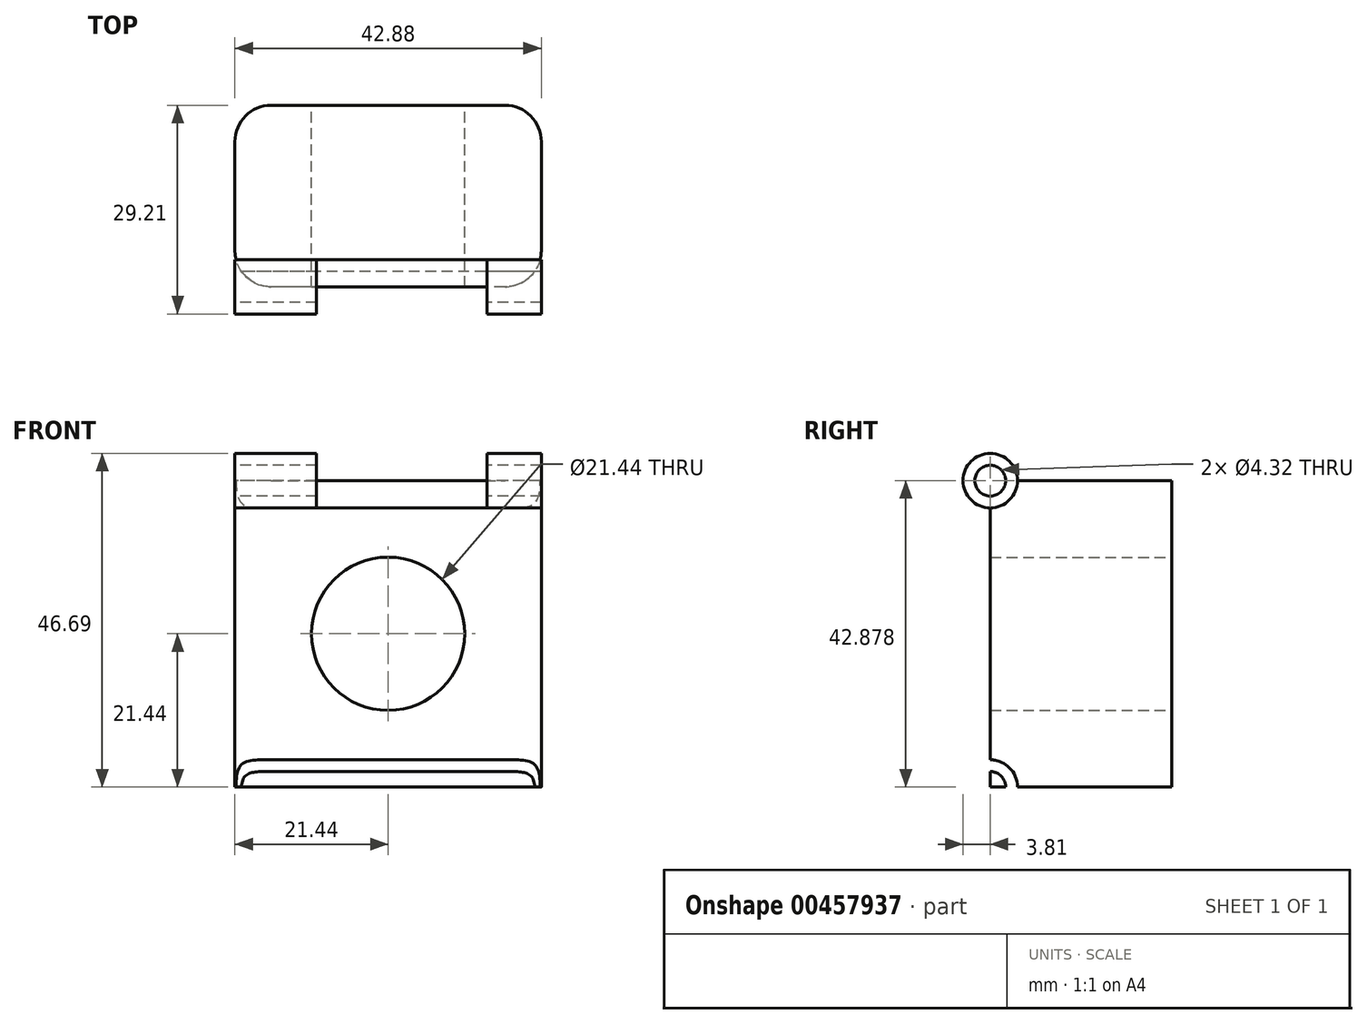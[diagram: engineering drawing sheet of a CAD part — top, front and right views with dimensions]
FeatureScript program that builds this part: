
annotation { "Feature Type Name" : "Feature", "Feature Type Description" : "" }
export const myFeature = defineFeature(function(context is Context, id is Id, definition is map)
    precondition{}
    {
        {
            var Q0;
            Q0=qCreatedBy(makeId("Front.planeOp"),FACE);
            var sketch = newSketch(context, id + "F0", { "sketchPlane" : qUnion([Q0])});
            skLineSegment(sketch, "E0.bottom", {"start": v(-21.44, 21.44) * mm, "end": v(21.44, 21.44) * mm});
            skLineSegment(sketch, "E0.top", {"start": v(-21.44, -21.44) * mm, "end": v(21.44, -21.44) * mm});
            skLineSegment(sketch, "E0.left", {"start": v(-21.44, 21.44) * mm, "end": v(-21.44, -21.44) * mm});
            skLineSegment(sketch, "E0.right", {"start": v(21.44, 21.44) * mm, "end": v(21.44, -21.44) * mm});
            skPoint(sketch, "E0.middle", {"position": v(0, 0) * mm});
            skCircle(sketch, "E1", {"center": v(0, 0) * mm, "radius": 10.72 * mm});
            skSolve(sketch);
        }
        {
            var Q0;
            Q0=makeQuery(id+"F0.imprint","IMPRINT",FACE,{"disambiguationData":[TD([[makeQuery(id+"F0.imprint","IMPRINT",EDGE,{"derivedFrom":sQuery(id+"F0.wireOp",EDGE,"E0.bottom")}),-1.0]])]});
            extrude(context, id + "F1", {"entities" : qUnion([Q0]), "depth" : 25.4 * mm, "offsetDistance" : 25.4 * mm});
        }
        {
            var Q0;
            Q0=makeQuery(id+"F1.opExtrude","CAP_EDGE",EDGE,{"disambiguationData":[OSD([sQuery(id+"F0.wireOp",EDGE,"E0.right")])],"isStart":true});
            var Q1;
            Q1=makeQuery(id+"F1.opExtrude","CAP_EDGE",EDGE,{"disambiguationData":[OSD([sQuery(id+"F0.wireOp",EDGE,"E0.right")])],"isStart":false});
            var Q2;
            Q2=makeQuery(id+"F1.opExtrude","CAP_EDGE",EDGE,{"disambiguationData":[OSD([sQuery(id+"F0.wireOp",EDGE,"E0.left")])],"isStart":true});
            var Q3;
            Q3=makeQuery(id+"F1.opExtrude","CAP_EDGE",EDGE,{"disambiguationData":[OSD([sQuery(id+"F0.wireOp",EDGE,"E0.left")])],"isStart":false});
            fillet(context, id + "F2", {"entities" : qUnion([Q0, Q1, Q2, Q3]), "radius" : 5.08 * mm, "tangentPropagation" : true, "allowEdgeOverflow" : false});
        }
        {
            var Q0;
            Q0=makeQuery(id+"F1.opExtrude","SWEPT_FACE",FACE,{"disambiguationData":[OSD([sQuery(id+"F0.wireOp",EDGE,"E0.left")])]});
            var sketch = newSketch(context, id + "F3", { "sketchPlane" : qUnion([Q0])});
            skPoint(sketch, "E2.0", {"position": v(25.4, 21.44) * mm});
            skPoint(sketch, "E3.0", {"position": v(25.4, -21.44) * mm});
            skCircle(sketch, "E4", {"center": v(25.4, 21.44) * mm, "radius": 3.81 * mm});
            skCircle(sketch, "E5.MirrorC", {"center": v(25.4, -21.44) * mm, "radius": 3.81 * mm});
            skCircle(sketch, "E6", {"center": v(25.4, 21.44) * mm, "radius": 2.16 * mm});
            skCircle(sketch, "E7.MirrorC", {"center": v(25.4, -21.44) * mm, "radius": 2.16 * mm});
            skSolve(sketch);
        }
        {
            var Q0;
            Q0 = qSketchRegion(id + "F3", true);
            var Q1;
            Q1=makeQuery(id+"F3.imprint","IMPRINT",FACE,{"disambiguationData":[TD([[makeQuery(id+"F3.imprint","IMPRINT",EDGE,{"derivedFrom":sQuery(id+"F3.wireOp",EDGE,"E6")}),1.0]])]});
            extrude(context, id + "F4", {"entities" : qUnion([Q0, Q1]), "operationType" : NewBodyOperationType.ADD, "oppositeDirection" : true, "depth" : 42.88 * mm, "offsetDistance" : 25.4 * mm});
        }
        {
            var Q0;
            Q0=makeQuery(id+"F3.imprint","IMPRINT",FACE,{"disambiguationData":[TD([[makeQuery(id+"F3.imprint","IMPRINT",EDGE,{"derivedFrom":sQuery(id+"F3.wireOp",EDGE,"E6")}),1.0]])]});
            extrude(context, id + "F5", {"entities" : qUnion([Q0]), "operationType" : NewBodyOperationType.REMOVE, "oppositeDirection" : true, "depth" : 47.98 * mm, "offsetDistance" : 25.4 * mm});
        }
        {
            var Q0;
            Q0 = qSketchRegion(id + "F3", true);
            extrude(context, id + "F6", {"entities" : qUnion([Q0]), "operationType" : NewBodyOperationType.REMOVE, "oppositeDirection" : true, "depth" : 35.26 * mm, "offsetDistance" : 25.4 * mm});
        }
        {
            var Q0;
            Q0 = qSketchRegion(id + "F3", true);
            extrude(context, id + "F7", {"entities" : qUnion([Q0]), "operationType" : NewBodyOperationType.ADD, "oppositeDirection" : true, "depth" : 11.43 * mm, "offsetDistance" : 25.4 * mm});
        }
        {
            var Q0;
            Q0=makeQuery(id+"F3.imprint","IMPRINT",FACE,{"disambiguationData":[TD([[makeQuery(id+"F3.imprint","IMPRINT",EDGE,{"derivedFrom":sQuery(id+"F3.wireOp",EDGE,"E7.MirrorC")}),-1.0]])]});
            extrude(context, id + "F8", {"entities" : qUnion([Q0]), "operationType" : NewBodyOperationType.REMOVE, "oppositeDirection" : true, "depth" : 58.17 * mm, "offsetDistance" : 25.4 * mm});
        }
    });
